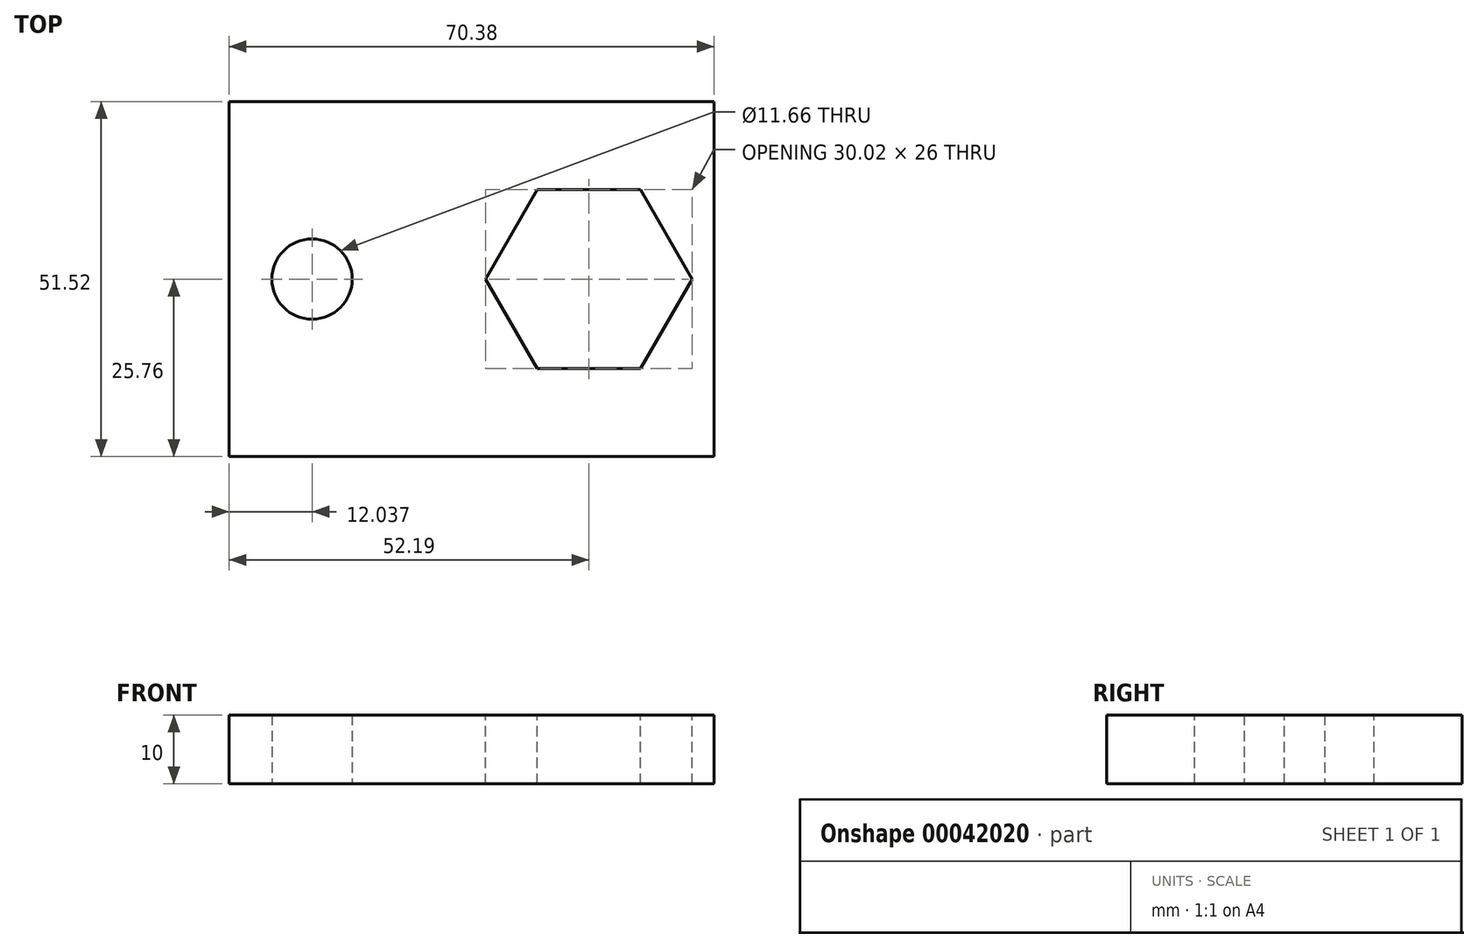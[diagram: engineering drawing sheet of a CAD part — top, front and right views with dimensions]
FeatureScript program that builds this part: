
annotation { "Feature Type Name" : "Feature", "Feature Type Description" : "" }
export const myFeature = defineFeature(function(context is Context, id is Id, definition is map)
    precondition{}
    {
        {
            var Q0;
            Q0=qCreatedBy(makeId("Top.planeOp"),FACE);
            var sketch = newSketch(context, id + "F0", { "sketchPlane" : qUnion([Q0])});
            skLineSegment(sketch, "E0.rect.bottom", {"start": v(-35.2, -25.76) * mm, "end": v(35.2, -25.76) * mm});
            skLineSegment(sketch, "E0.rect.top", {"start": v(-35.2, 25.76) * mm, "end": v(35.2, 25.76) * mm});
            skLineSegment(sketch, "E0.rect.left", {"start": v(-35.2, -25.76) * mm, "end": v(-35.2, 25.76) * mm});
            skLineSegment(sketch, "E0.rect.right", {"start": v(35.2, -25.76) * mm, "end": v(35.2, 25.76) * mm});
            skPoint(sketch, "E0.rect.middle", {"position": v(0, 0) * mm});
            skLineSegment(sketch, "E1", {"start": v(-35.2, 0) * mm, "end": v(35.2, 0) * mm, "construction": true});
            skCircle(sketch, "E2", {"center": v(-23.15, 0) * mm, "radius": 5.83 * mm});
            skSolve(sketch);
        }
        {
            var Q0;
            Q0=makeQuery(id+"F0.imprint","IMPRINT",FACE,{"disambiguationData":[TD([[makeQuery(id+"F0.imprint","IMPRINT",EDGE,{"derivedFrom":sQuery(id+"F0.wireOp",EDGE,"E0.rect.bottom")}),1.0]])]});
            extrude(context, id + "F1", {"entities" : qUnion([Q0]), "endBound" : BoundingType.SYMMETRIC, "depth" : 10 * mm});
        }
        {
            var Q0;
            Q0=makeQuery(id+"F1.opExtrude","CAP_FACE",FACE,{"disambiguationData":[OSD([sQuery(id+"F0.wireOp",EDGE,"E0.rect.bottom"),sQuery(id+"F0.wireOp",EDGE,"E0.rect.top"),sQuery(id+"F0.wireOp",EDGE,"E0.rect.left"),sQuery(id+"F0.wireOp",EDGE,"E0.rect.right"),sQuery(id+"F0.wireOp",EDGE,"E2")])],"isStart":false});
            var sketch = newSketch(context, id + "F2", { "sketchPlane" : qUnion([Q0])});
            skCircle(sketch, "E3.cCircle", {"center": v(17, 0) * mm, "radius": 13 * mm, "construction": true});
            skLineSegment(sketch, "E3.0", {"start": v(9.5, 13) * mm, "end": v(24.5, 13) * mm});
            skLineSegment(sketch, "E3.1", {"start": v(24.5, 13) * mm, "end": v(32.01, 0) * mm});
            skLineSegment(sketch, "E3.2", {"start": v(32.01, 0) * mm, "end": v(24.5, -13) * mm});
            skLineSegment(sketch, "E3.3", {"start": v(24.5, -13) * mm, "end": v(9.5, -13) * mm});
            skLineSegment(sketch, "E3.4", {"start": v(9.5, -13) * mm, "end": v(1.99, 0) * mm});
            skLineSegment(sketch, "E3.5", {"start": v(1.99, 0) * mm, "end": v(9.5, 13) * mm});
            skPoint(sketch, "E3.0.midPoint", {"position": v(17, 13) * mm});
            skSolve(sketch);
        }
        {
            var Q0;
            Q0=makeQuery(id+"F2.imprint","IMPRINT",FACE,{"disambiguationData":[TD([[makeQuery(id+"F2.imprint","IMPRINT",EDGE,{"derivedFrom":sQuery(id+"F2.wireOp",EDGE,"E3.0")}),-1.0]])]});
            extrude(context, id + "F3", {"entities" : qUnion([Q0]), "operationType" : NewBodyOperationType.REMOVE, "oppositeDirection" : true, "depth" : 25 * mm});
        }
    });
